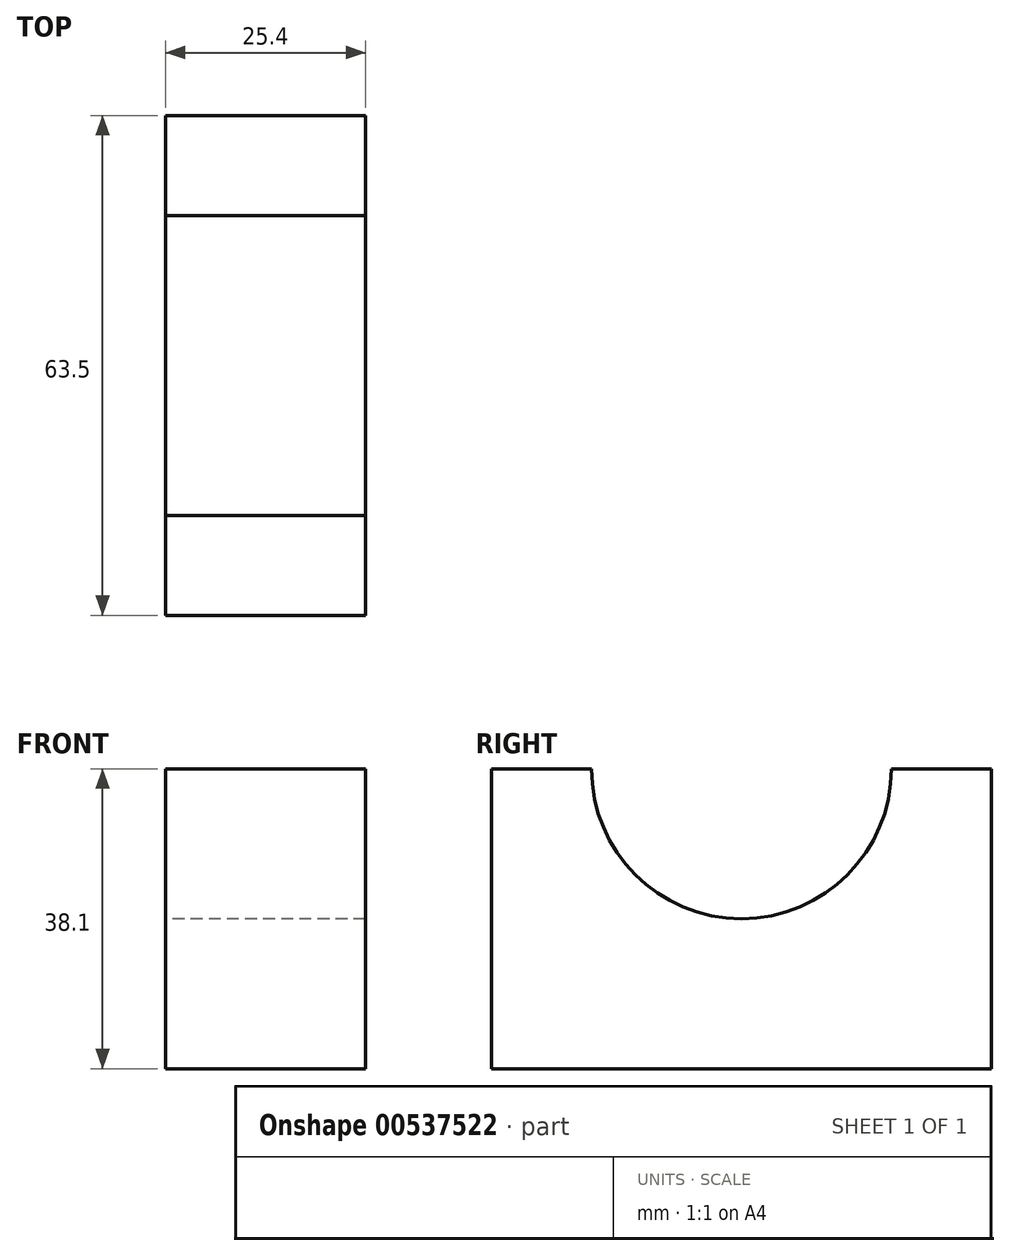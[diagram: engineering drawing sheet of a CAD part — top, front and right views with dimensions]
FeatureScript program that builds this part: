
annotation { "Feature Type Name" : "Feature", "Feature Type Description" : "" }
export const myFeature = defineFeature(function(context is Context, id is Id, definition is map)
    precondition{}
    {
        {
            var Q0;
            Q0=qCreatedBy(makeId("Right.planeOp"),FACE);
            var sketch = newSketch(context, id + "F0", { "sketchPlane" : qUnion([Q0])});
            skLineSegment(sketch, "E0", {"start": v(0, 0) * mm, "end": v(0, 38.1) * mm});
            skLineSegment(sketch, "E1", {"start": v(0, 0) * mm, "end": v(-63.5, 0) * mm});
            skLineSegment(sketch, "E2", {"start": v(-63.5, 0) * mm, "end": v(-63.5, 38.1) * mm});
            skLineSegment(sketch, "E3", {"start": v(-63.5, 38.1) * mm, "end": v(-50.8, 38.1) * mm});
            skLineSegment(sketch, "E4", {"start": v(0, 38.1) * mm, "end": v(-12.7, 38.1) * mm});
            skArc(sketch, "E5", {"start": v(-50.8, 38.1) * mm, "mid": v(-31.75, 19.05) * mm, "end": v(-12.7, 38.1) * mm});
            skSolve(sketch);
        }
        {
            var Q0;
            Q0 = qSketchRegion(id + "F0", true);
            extrude(context, id + "F1", {"entities" : qUnion([Q0]), "depth" : 25.4 * mm, "offsetDistance" : 25.4 * mm});
        }
    });
